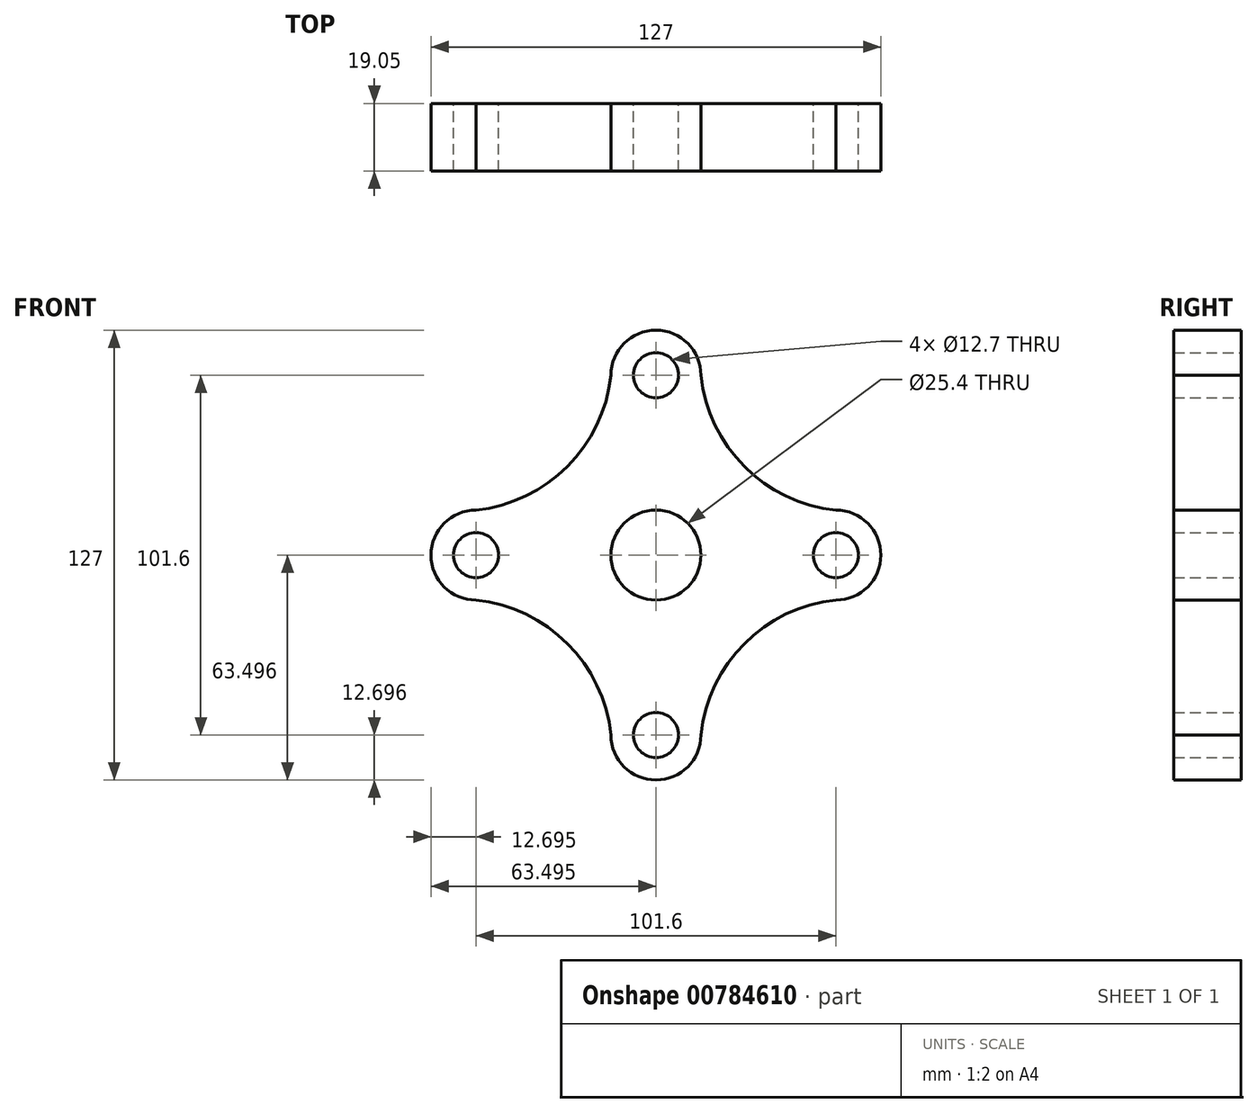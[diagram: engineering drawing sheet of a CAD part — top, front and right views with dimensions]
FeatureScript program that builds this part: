
annotation { "Feature Type Name" : "Feature", "Feature Type Description" : "" }
export const myFeature = defineFeature(function(context is Context, id is Id, definition is map)
    precondition{}
    {
        {
            var Q0;
            Q0=qCreatedBy(makeId("Front.planeOp"),FACE);
            var sketch = newSketch(context, id + "F0", { "sketchPlane" : qUnion([Q0])});
            skCircle(sketch, "E0", {"center": v(-51.08, 0.48) * mm, "radius": 6.35 * mm});
            skCircle(sketch, "E1", {"center": v(50.52, 0.48) * mm, "radius": 6.35 * mm});
            skCircle(sketch, "E2", {"center": v(-0.28, 0.48) * mm, "radius": 12.7 * mm});
            skCircle(sketch, "E3", {"center": v(-0.28, -50.32) * mm, "radius": 6.35 * mm});
            skCircle(sketch, "E4", {"center": v(-0.28, 51.28) * mm, "radius": 6.35 * mm});
            skArc(sketch, "E5", {"start": v(-51.08, 13.18) * mm, "mid": v(-25.31, 25.5) * mm, "end": v(-12.98, 51.28) * mm});
            skArc(sketch, "E6", {"start": v(12.42, 51.28) * mm, "mid": v(-0.28, 63.98) * mm, "end": v(-12.98, 51.28) * mm});
            skArc(sketch, "E7", {"start": v(-51.08, 13.18) * mm, "mid": v(-63.78, 0.48) * mm, "end": v(-51.08, -12.22) * mm});
            skPoint(sketch, "E8.trimOffspring.end.orphan", {"position": v(-51.08, 51.28) * mm});
            skArc(sketch, "E9", {"start": v(12.42, 51.28) * mm, "mid": v(24.7, 25.46) * mm, "end": v(50.52, 13.18) * mm});
            skArc(sketch, "E10", {"start": v(50.52, -12.22) * mm, "mid": v(63.22, 0.48) * mm, "end": v(50.52, 13.18) * mm});
            skPoint(sketch, "E11.orphan", {"position": v(50.52, 51.28) * mm});
            skArc(sketch, "E12", {"start": v(50.52, -12.22) * mm, "mid": v(24.7, -24.5) * mm, "end": v(12.42, -50.32) * mm});
            skArc(sketch, "E13", {"start": v(-12.98, -50.32) * mm, "mid": v(-0.28, -63.02) * mm, "end": v(12.42, -50.32) * mm});
            skArc(sketch, "E14", {"start": v(-12.98, -50.32) * mm, "mid": v(-25.27, -24.5) * mm, "end": v(-51.08, -12.22) * mm});
            skPoint(sketch, "E15.orphan", {"position": v(-51.08, -50.32) * mm});
            skPoint(sketch, "E16.orphan", {"position": v(50.52, -50.32) * mm});
            skSolve(sketch);
        }
        {
            var Q0;
            Q0 = qSketchRegion(id + "F0", true);
            extrude(context, id + "F1", {"entities" : qUnion([Q0]), "depth" : 19.05 * mm, "offsetDistance" : 25.4 * mm});
        }
    });
